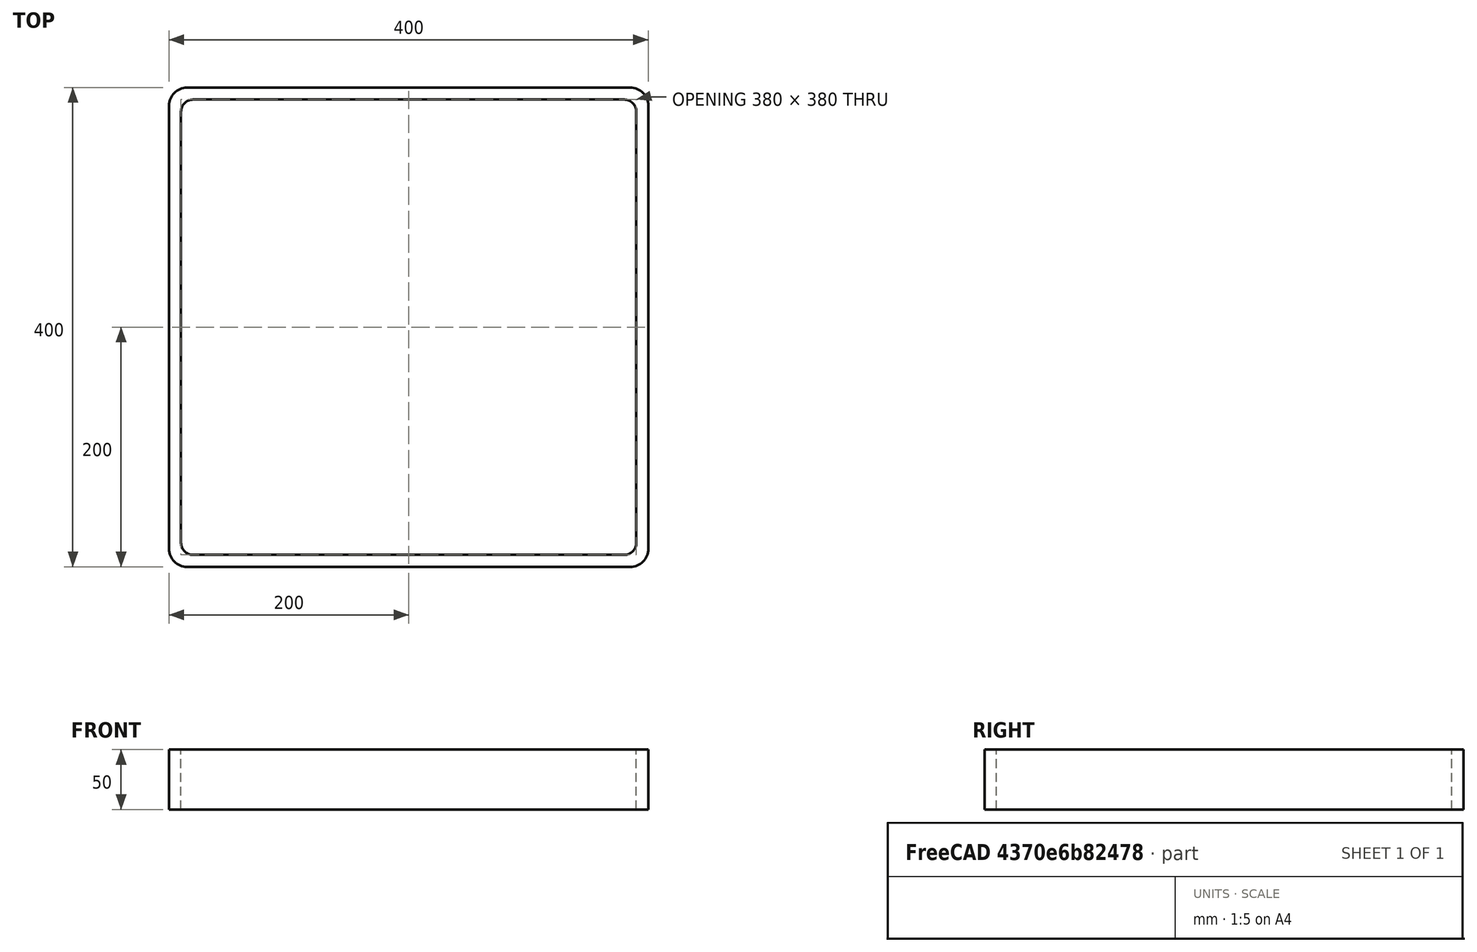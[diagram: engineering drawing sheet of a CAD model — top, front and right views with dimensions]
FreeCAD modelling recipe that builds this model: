
FCSTD DOCUMENT  (FreeCAD 0.15R4671 (Git))
Label: Square hollow section 400x400x10 EN10219 S235JRH
License: All rights reserved
LicenseURL: http://en.wikipedia.org/wiki/All_rights_reserved
objects: Sketcher::SketchObject×1, Part::Extrusion×1
note: 2 computed .brp shape members not serialized (recipe doc carries the construction recipe); baked Part::Feature solids carry a one-line shape summary decoded from their .brp

FEATURE [Sketcher::SketchObject] Sketch
  sketch-geometry (16):
    g0: LineSegment StartX=-180 StartY=190 StartZ=0 EndX=180 EndY=190 EndZ=0
    g1: LineSegment StartX=190 StartY=180 StartZ=0 EndX=190 EndY=-180 EndZ=0
    g2: LineSegment StartX=180 StartY=-190 StartZ=0 EndX=-180 EndY=-190 EndZ=0
    g3: LineSegment StartX=-190 StartY=-180 StartZ=0 EndX=-190 EndY=180 EndZ=0
    g4: LineSegment StartX=-185 StartY=200 StartZ=0 EndX=185 EndY=200 EndZ=0
    g5: LineSegment StartX=200 StartY=185 StartZ=0 EndX=200 EndY=-185 EndZ=0
    g6: LineSegment StartX=185 StartY=-200 StartZ=0 EndX=-185 EndY=-200 EndZ=0
    g7: LineSegment StartX=-200 StartY=-185 StartZ=0 EndX=-200 EndY=185 EndZ=0
    g8: ArcOfCircle CenterX=-180 CenterY=180 CenterZ=0 NormalX=0 NormalY=0 NormalZ=1 Radius=10 StartAngle=1.5708 EndAngle=3.14159
    g9: ArcOfCircle CenterX=180 CenterY=180 CenterZ=0 NormalX=0 NormalY=0 NormalZ=1 Radius=10 StartAngle=0 EndAngle=1.5708
    g10: ArcOfCircle CenterX=180 CenterY=-180 CenterZ=0 NormalX=0 NormalY=0 NormalZ=1 Radius=10 StartAngle=4.71239 EndAngle=6.28319
    g11: ArcOfCircle CenterX=-180 CenterY=-180 CenterZ=0 NormalX=0 NormalY=0 NormalZ=1 Radius=10 StartAngle=3.14159 EndAngle=4.71239
    g12: ArcOfCircle CenterX=185 CenterY=185 CenterZ=0 NormalX=0 NormalY=0 NormalZ=1 Radius=15 StartAngle=0 EndAngle=1.5708
    g13: ArcOfCircle CenterX=185 CenterY=-185 CenterZ=0 NormalX=0 NormalY=0 NormalZ=1 Radius=15 StartAngle=4.71239 EndAngle=6.28319
    g14: ArcOfCircle CenterX=-185 CenterY=-185 CenterZ=0 NormalX=0 NormalY=0 NormalZ=1 Radius=15 StartAngle=3.14159 EndAngle=4.71239
    g15: ArcOfCircle CenterX=-185 CenterY=185 CenterZ=0 NormalX=0 NormalY=0 NormalZ=1 Radius=15 StartAngle=1.5708 EndAngle=3.14159
  constraints (36):
    c: Horizontal(g2)
    c: Vertical(g3)
    c: Horizontal(g6)
    c: Vertical(g7)
    c: Tangent(g3,g8) = 1.5708
    c: Tangent(g0,g8) = 1.5708
    c: Tangent(g0,g9) = 1.5708
    c: Tangent(g1,g9) = 1.5708
    c: Tangent(g1,g10) = 1.5708
    c: Tangent(g2,g10) = 1.5708
    c: Tangent(g2,g11) = 1.5708
    c: Tangent(g3,g11) = 1.5708
    c: Tangent(g4,g12) = 1.5708
    c: Tangent(g5,g12) = 1.5708
    c: Tangent(g5,g13) = 1.5708
    c: Tangent(g6,g13) = 1.5708
    c: Tangent(g6,g14) = 1.5708
    c: Tangent(g7,g14) = 1.5708
    c: Tangent(g7,g15) = 1.5708
    c: Tangent(g4,g15) = 1.5708
    c: Equal(g9,g8)
    c: Equal(g9,g11)
    c: Equal(g9,g10)
    c: Equal(g12,g15)
    c: Equal(g12,g14)
    c: Equal(g12,g13)
    c: Symmetric(g4,g6,g-1)
    c: Symmetric(g7,g5,g-2)
    c: DistanceY(g4,g6) = -400
    c: DistanceX(g7,g5) = 400
    c: Symmetric(g3,g1,g-2)
    c: Symmetric(g0,g2,g-1)
    c: DistanceY(g0,g4) = 10
    c: DistanceX(g5,g1) = -10
    c: Radius(g9) = 10
    c: Radius(g12) = 15
FEATURE [Part::Extrusion] Extrude  label="Square hollow section 400x400x10 EN10219 S235JRH"
  Base = -> Sketch
  Dir = (0,0,50)
  Solid = true
